# Revit family: TPOne-M_B_FR_RFA
name_source: partatom
category: Data Devices
revit_build: Autodesk Revit 2017 (Build: 20161205_1400(x64)
units: mm (PartAtom-declared; Revit-internal decimal feet)

## family parameters
Cut with Voids When Loaded = No
Host = Face
Maintain Annotation Orientation = Yes
Part Type = Normal
Room Calculation Point = No
Round Connector Dimension = Use Diameter
Shared = No

## types (3) — shared parameters
D = 30 mm  [stored 0.0984252 ft]
D-All = 9 mm
D1a = 6 mm  [stored 0.019685 ft]
D1b = 3 mm  [stored 0.00984252 ft]
D2 = 11 mm  [stored 0.0360892 ft]
Da = 1 mm  [stored 0.00328084 ft]
Default Elevation = 1219 mm
H1_2 = 30 mm  [stored 0.0984252 ft]
H2_2 = 24 mm
H_2 = 33 mm  [stored 0.108268 ft]
IP Rating = IP20
IfcExportAs = IfcElectricApplianceType
IfcExportType = Controller
Manufacturer = Danfoss
Operating Temperature Range = 0-45 C
Setting Temperature Range = 5-35 C
URL = https://assets.danfoss.com
W1_2 = 74 mm
W2_2 = 68 mm
W_2 = 78 mm

## per-type parameters (varying)
| type | Description | Maximum Range | Model | Model Type | Operating Frequency | Output Channel 1 | Output Channel 2 | Power Supply RT | RX1-S | Switch Rating Channel 1 |
| TPOne-B_087N7851 | TPOne-B | - | 087N7851 | Programmable Thermostat | - | Volt free, SPDT type 1B | - | 2.5-3VDC (2x AA Alkaline Batteries) | No | 3A at 230Vac |
| TPOne-M_087N7852 | TPOne-M | - | 087N7852 | Programmable Thermostat | - | Volt free, SPDT type 1B | 3A at 230Vac | 230 Vac, 50/60Hz | No | 3A at 230Vac |
| TPOne-RF + RX1-S_087N7854 | TPOne-RF + RX1-S | 30 m | 087N7854 | RF Programmable Thermostat | 43.92 Mhz | Volt free, SPDT type 1B (RX1-S) | - | 2.5-3VDC (2x AA Alkaline Batteries) | Yes | 3A at 230Vac (RX1-S) |

note: [stored X ft] marks values corroborated as IEEE doubles in the binary element streams (Revit-internal decimal feet)

## geometry (parser evidence)
native form markers: Sweep x5
no freeform markers — native parametric forms only
